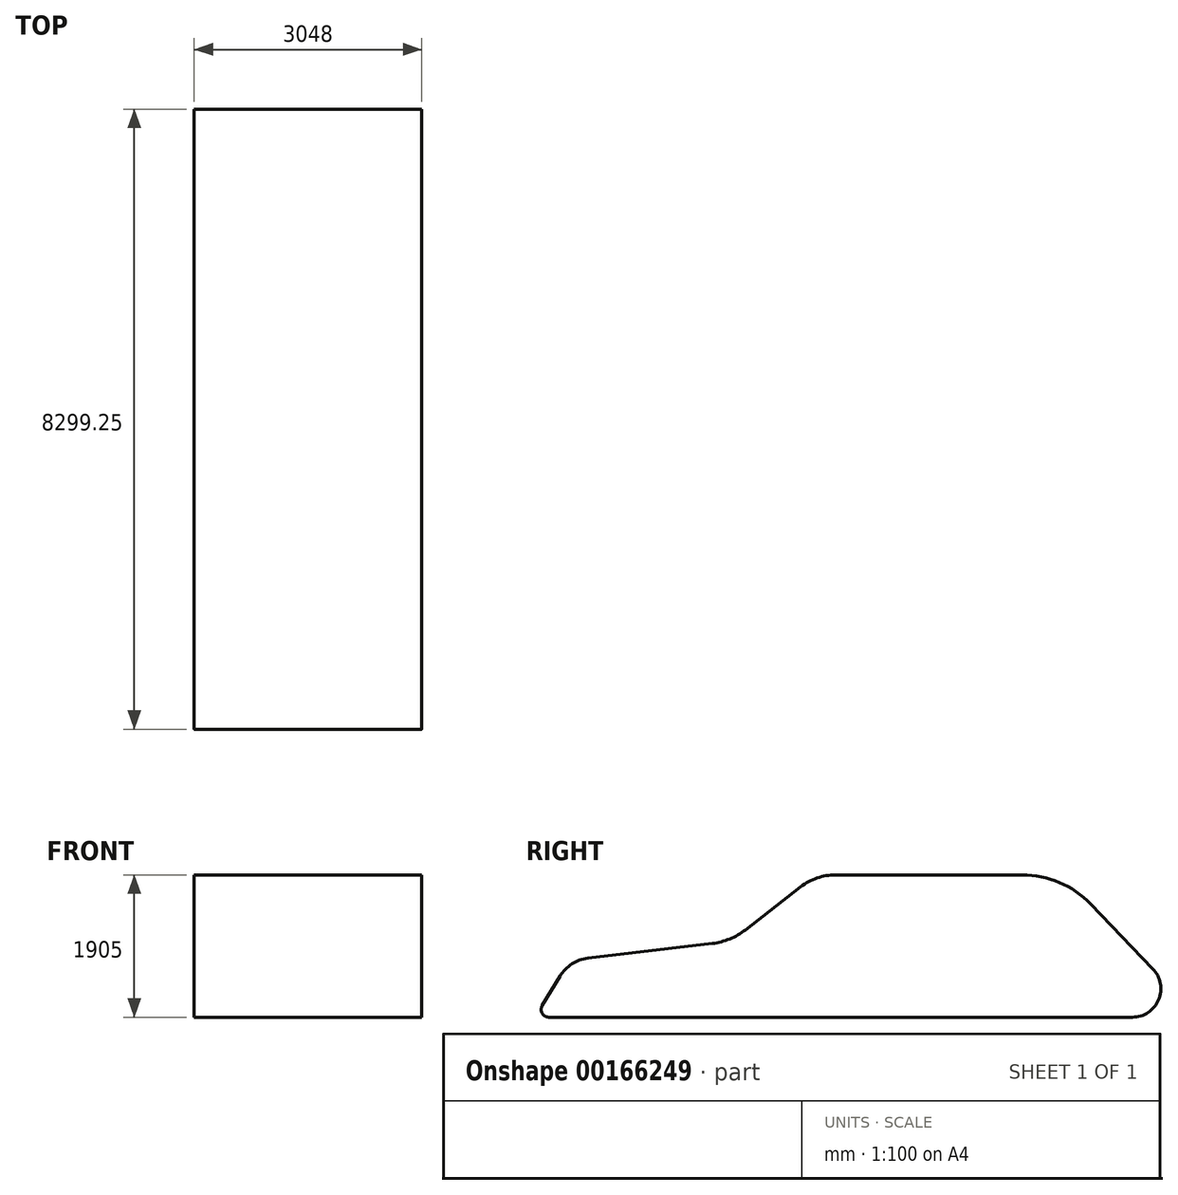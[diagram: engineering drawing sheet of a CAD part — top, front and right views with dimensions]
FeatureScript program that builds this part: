
annotation { "Feature Type Name" : "Feature", "Feature Type Description" : "" }
export const myFeature = defineFeature(function(context is Context, id is Id, definition is map)
    precondition{}
    {
        {
            var Q0;
            Q0=qCreatedBy(makeId("Front.planeOp"),FACE);
            var sketch = newSketch(context, id + "F0", { "sketchPlane" : qUnion([Q0])});
            skLineSegment(sketch, "E0", {"start": v(0, -1143) * mm, "end": v(1407.05, -1143) * mm, "construction": true});
            skLineSegment(sketch, "E1", {"start": v(494.4, 0) * mm, "end": v(1594.53, 0) * mm});
            skLineSegment(sketch, "E2.top", {"start": v(1130.3, -621.68) * mm, "end": v(1409.7, -621.68) * mm});
            skPoint(sketch, "E3.visualSharp", {"position": v(1078.15, -621.68) * mm});
            skLineSegment(sketch, "E4", {"start": v(1079.5, -529.74) * mm, "end": v(1079.5, -570.88) * mm});
            skPoint(sketch, "E5.visualSharp", {"position": v(1079.5, -621.68) * mm});
            skArc(sketch, "E5.filletArc", {"start": v(1079.5, -570.88) * mm, "mid": v(1094.38, -606.8) * mm, "end": v(1130.3, -621.68) * mm});
            skLineSegment(sketch, "E6", {"start": v(1460.5, -570.88) * mm, "end": v(1460.5, -529.74) * mm});
            skPoint(sketch, "E7.visualSharp", {"position": v(1460.5, -621.68) * mm});
            skArc(sketch, "E7.filletArc", {"start": v(1409.7, -621.68) * mm, "mid": v(1445.62, -606.8) * mm, "end": v(1460.5, -570.88) * mm});
            skPoint(sketch, "E8.visualSharp", {"position": v(1079.5, -489.77) * mm});
            skArc(sketch, "E9.filletArc", {"start": v(1130.3, -478.94) * mm, "mid": v(1094.38, -493.81) * mm, "end": v(1079.5, -529.74) * mm});
            skPoint(sketch, "E10.visualSharp", {"position": v(1460.5, -489.77) * mm});
            skArc(sketch, "E10.filletArc", {"start": v(1460.5, -529.74) * mm, "mid": v(1445.62, -493.81) * mm, "end": v(1409.7, -478.94) * mm});
            skArc(sketch, "E11", {"start": v(1409.7, -478.94) * mm, "mid": v(1270, -469.28) * mm, "end": v(1130.3, -478.94) * mm});
            skSolve(sketch);
        }
        {
            var Q0;
            Q0=qCreatedBy(makeId("Right.planeOp"),FACE);
            var sketch = newSketch(context, id + "F1", { "sketchPlane" : qUnion([Q0])});
            skLineSegment(sketch, "E12", {"start": v(179.44, 0) * mm, "end": v(7996.1, 0) * mm});
            skLineSegment(sketch, "E13", {"start": v(92.32, 153.87) * mm, "end": v(328.8, 548) * mm});
            skPoint(sketch, "E14.visualSharp", {"position": v(0, 0) * mm});
            skArc(sketch, "E14.filletArc", {"start": v(92.32, 153.87) * mm, "mid": v(91.03, 51.54) * mm, "end": v(179.44, 0) * mm});
            skLineSegment(sketch, "E15", {"start": v(705.05, 791.16) * mm, "end": v(2369.98, 987.03) * mm});
            skPoint(sketch, "E16.visualSharp", {"position": v(457.2, 762) * mm});
            skArc(sketch, "E16.filletArc", {"start": v(705.05, 791.16) * mm, "mid": v(488.68, 713.3) * mm, "end": v(328.8, 548) * mm});
            skLineSegment(sketch, "E17", {"start": v(2811.9, 1168.2) * mm, "end": v(3552.83, 1744.49) * mm});
            skPoint(sketch, "E18.visualSharp", {"position": v(2616.2, 1016) * mm});
            skArc(sketch, "E18.filletArc", {"start": v(2369.98, 987.03) * mm, "mid": v(2603.33, 1047.39) * mm, "end": v(2811.9, 1168.2) * mm});
            skLineSegment(sketch, "E19", {"start": v(4020.65, 1905) * mm, "end": v(6519.9, 1905) * mm});
            skPoint(sketch, "E20.visualSharp", {"position": v(3759.2, 1905) * mm});
            skArc(sketch, "E20.filletArc", {"start": v(4020.65, 1905) * mm, "mid": v(3773.35, 1863.76) * mm, "end": v(3552.83, 1744.49) * mm});
            skLineSegment(sketch, "E21", {"start": v(7436.07, 1514.52) * mm, "end": v(8270.94, 644.85) * mm});
            skPoint(sketch, "E22.visualSharp", {"position": v(7061.2, 1905) * mm});
            skArc(sketch, "E22.filletArc", {"start": v(7436.07, 1514.52) * mm, "mid": v(7017.86, 1803.3) * mm, "end": v(6519.9, 1905) * mm});
            skPoint(sketch, "E23.visualSharp", {"position": v(8890, 0) * mm});
            skArc(sketch, "E23.filletArc", {"start": v(7996.1, 0) * mm, "mid": v(8346.58, 231.61) * mm, "end": v(8270.94, 644.85) * mm});
            skSolve(sketch);
        }
        {
            var Q0;
            Q0=makeQuery(id+"F1.imprint","IMPRINT",FACE,{"disambiguationData":[TD([[makeQuery(id+"F1.imprint","IMPRINT",EDGE,{"derivedFrom":sQuery(id+"F1.wireOp",EDGE,"E12")}),1.0]])]});
            extrude(context, id + "F2", {"entities" : qUnion([Q0]), "depth" : 3048 * mm});
        }
    });
